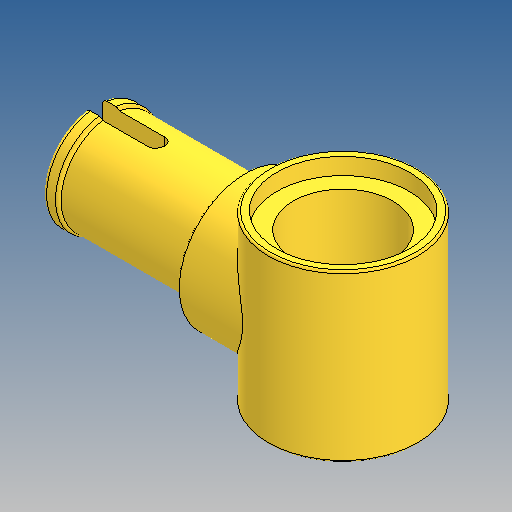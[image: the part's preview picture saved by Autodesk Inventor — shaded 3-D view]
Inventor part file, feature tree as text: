
AUTODESK INVENTOR PART (.ipt)
format: ipt  version: 2025 (Build 290162010, 162A)  size: 240,640 bytes
history: native  units: mm
features: extrude x4, sketch x4, mirror x1, revolve x1, fillet x1, projected_geometry x1
ambient origin geometry x8: Origin, YZ Plane, XZ Plane, XY Plane, X Axis, Y Axis, Z Axis, Center Point
bodies: Solid1 (feature_tree)
feature tree (12):
  extrude  "Extrusion1"  Depth=0.8mm TaperAngle=0.0deg
  extrude  "Extrusion7"  Depth=6.4mm
  mirror  "Mirror1"
  sketch  "Sketch7"  dims[d50=4.8mm d53=7.2mm]
  revolve  "Revolution1"  [1 undecoded]
  extrude  "Extrusion9"  Depth=0.2mm
  extrude  "Extrusion10"  Depth=0.2mm
  fillet  "Fillet2"  Radius=0.8mm
  sketch  "Sketch1"  dims[d14=8.0mm d15=0.0mm d41=0.8mm d42=0.0mm]
  sketch  "Sketch6"  dims[d48=7.2mm d49=6.4mm]
  sketch  "Sketch8"  dims[d54=0.8mm d55=4.8mm d58=3.4mm d59=0.8mm d60=90.0deg d62=6.4mm d63=3.2mm d64=5.0mm d65=4.8mm d66=10.0mm d67=0.0mm d68=10.0mm d69=0.0mm d70=0.1mm d71=0.0mm d73=0.2mm]
  projected_geometry  "Projected Loop3"
note: 1 required parameter value undecoded (feature->parameter linkage not recoverable at this tier; creation-order binding heuristic only, values carry confidence <= 0.55)
